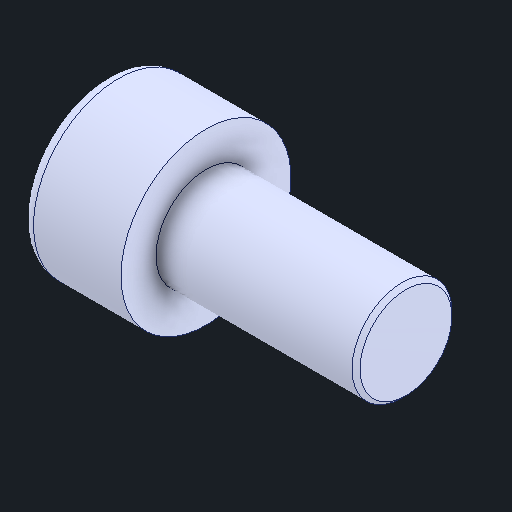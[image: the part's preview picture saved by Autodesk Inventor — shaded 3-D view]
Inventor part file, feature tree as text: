
AUTODESK INVENTOR PART (.ipt)
format: ipt  version: 2025 (Build 290162000, 162)  size: 133,120 bytes
history: native  units: mm
features: chamfer x1
ambient origin geometry x8: Origin, YZ Plane, XZ Plane, XY Plane, X Axis, Y Axis, Z Axis, Center Point
bodies: 实体1 (feature_tree)
feature tree (1):
  chamfer  "Chamfer1"  [1 undecoded]
note: 1 required parameter value undecoded (feature->parameter linkage not recoverable at this tier; creation-order binding heuristic only, values carry confidence <= 0.55)
